# Revit family: Planet-Wattohm boites de sol universelles affleurantes
name_source: partatom
category: Installations électriques
units: mm (PartAtom-declared; Revit-internal decimal feet)

## family parameters
Conserver l'orientation des annotations = Non
Cote de connecteur circulaire = Utiliser le diamètre
Couper avec des vides une fois chargée = Non
Hôte = Face
Partagée = Non
Point de calcul de pièce = Non
Type d'élément = Normal

## types (9) — shared parameters
00 = Reservation boitier : 00
000000 = Accessoire : None
01 = Reservation boitier : 01
02 = Reservation boitier : 02
26 = Reservation boitier : 26
27 = Reservation boitier : 27
28 = Reservation boitier : 28
80 = Reservation boitier : 80
90 = Reservation boitier : 90
91 = Reservation boitier : 91
92 = Reservation boitier : 92
Auto = Type de sol utilisé : Auto ajustable
Brass = Finition : Laiton
Fabricant = LEGRAND
Inox = Finition : Acier inoxydable
PW-28500 = Boitier d'encastrement : PW-28500
PW-28501 = Accessoire : PW-28501
PW-28502 = Accessoire : PW-28502
PW-28503 = Accessoire : PW-28503
PW-28510 = Accessoire : PW-28510 + PW-28511+PW-28601
PW-28510-2 = Accessoire : PW-28510 + (2xPW-28511)+PW-28601
PW-28512 = Boitier d'encastrement : PW-28512
PW-28514 = Accessoire : PW-28514
PW-28516 = Accessoire : PW-28516
PW-28518 = Boitier d'encastrement : PW-28518
PW-28524 = Boitier d'encastrement : PW-28524
PW-28528 = Accessoire : PW-28528
PW-28771 = Plaque finition : PW-28771
PW-28773 = Plaque finition : PW-28773
PW-28781 = Plaque finition : PW-28781
PW-28783 = Plaque finition : PW-28783
PW-28791 = Plaque finition : PW-28791
PW-28793 = Plaque finition : PW-28793
PW-28901 = Couvercle : PW-28901
PW-28903 = Couvercle : PW-28903
PW-28911 = Couvercle : PW-28911
PW-28913 = Couvercle : PW-28913
PW-28921 = Couvercle : PW-28921
PW-28923 = Couvercle : PW-28923
StdB125 = Type de sol utilisé : Plancher béton inférieur 125 mm
StdB170 = Type de sol utilisé : Plancher béton entre 125 mm et 170 mm
StdB250 = Type de sol utilisé : Plancher béton entre 170 mm et 250 mm
StdT = Type de sol utilisé : Plancher technique
zero-valued in all types: Elévation par défaut

## per-type parameters (varying)
| type | Description | Support | Support appareillage | Supports |
| 8 modules 2x4 | Boite de sol universelle affleurante 8 modules vertical | 23 | Support appareillage : PW-28652 | PW-28652 |
| 12 modules 2x6 | Boite de sol universelle affleurante 12 modules vertical | 24 | Support appareillage : PW-28658 | PW-28658 |
| 16 modules 2x8 | Boite de sol universelle affleurante 16 modules vertical | 25 | Support appareillage : PW-28654 | PW-28654 |
| 12 modules 3x4 | Boite de sol universelle affleurante 12 modules horizontal ajustable | 20 | Support appareillage : PW-28662 | PW-28662 |
| 18 modules 3x6 | Boite de sol universelle affleurante 18 modules horizontal ajustable | 21 | Support appareillage : PW-28668 | PW-28668 |
| 24 modules 3x8 | Boite de sol universelle affleurante 24 modules horizontal ajustable | 22 | Support appareillage : PW-28664 | PW-28664 |
| Trappe de visite 8-12 modules | Trappe de visite couvercle affleurante 8/12 modules | 39 | Support appareillage : PW-28629 | PW-28629 |
| Trappe de visite 12-18 modules | Trappe de visite couvercle affleurante 12/18 modules | 40 | Support appareillage : PW-28630 | PW-28630 |
| Trappe de visite 16-24 modules | Trappe de visite couvercle affleurante 16/24 modules | 41 | Support appareillage : PW-28631 | PW-28631 |
